# Revit family: NXRCFCX
name_source: partatom
category: Communication Devices
revit_build: Autodesk Revit 2014 (Build: 20130308_1515(x64)
units: mm (PartAtom-declared; Revit-internal decimal feet)

## types (1)
- NXRCFCX
    Assembly Code = D5090
    Certification = Conforms with UL916 and Certified to CAN/
CSA C22.2 No. 205-M1983
• IC Approved
• Title 24 compliance
    Default Elevation = 0 "
    Description = The FX enabled NX Room Controller (NXRCFX) provides automatic and manual lighting control with the simplicity of plug-in installation and auto-configuration. Devices such as digital wall stations, occupancy/vacancy sensors, and daylight sensors are simply plugged into the FX Room Controller and auto-configure to default operations. All device communication is over stardard Cat5 cables which simplifies installation and eliminates wiring errors. Advanced configuration of the FX Room Controller can be accomplished through use of the NX Bluetooth® Radio and free controlHUBB mobile application available for both Android™ and iOS® devices. All of these features add up to an efficient, user-friendly and trouble-free installation.
    Dimming = Class 2/Class 1
• Installation as Class 1 requires 600 volt
insulation on dimming conductors sharing
a conduit with line voltage conductors
    Features = • Single or dual relay versions for ON/OFF or bi-level control
• Approved for use with controlled receptacles
• Single or dual 0-10V interface for full range dimming control
• FX bus enabled, allows for up to 32 room controllers per NX Zone Segment
• SmartPORT™ auto configuration support for NX Occupancy Sensors,
Daylight Sensors and Smart Wall Stations
• Intelligently and automatically responds to sensors and switches in the most
efficient manner
• Schedules are held in the devices themselves with integral Time Clock
requiring no additional devices for scheduling
• Advanced configuration, power metering, and control through either NX
Area Controller or HCS controlHUBB Bluetooth™ mobile application
    Housing Material = Plastic - Hubbell - Gray
    L = 5.26 "
    Manufacturer = Hubbell Control Solutions
    Model = NX Room Controller
    Product Documentation Link = https://hubbellcdn.com
    Product Page URL = https://www.hubbell.com
    Standby Power = 120VAC: 1.2,277VAC: 1.5,347VAC: 1.5
    Type Comments = FX Room Controller
    URL = https://www.hubbell.com
    Voltage = 120/277/347 VAC
    Warranty = 5-Years Warranty
    Washer = Metal-Hubbell-Galvanized_Steel

## geometry (parser evidence)
native form markers: Sweep x1
no freeform markers — native parametric forms only
